# Revit family: Toilet_Seat-Elongated_Closed_Front-KOHLER-EIR-K-79208
name_source: partatom
category: Specialty Equipment
units: mm (PartAtom-declared; Revit-internal decimal feet)

## family parameters
Cut with Voids When Loaded = No
Host = Face
OmniClass Number = 23.31.19.19.17
OmniClass Title = Water Closet Seats
Part Type = Normal
Room Calculation Point = No
Round Connector Dimension = Use Diameter
Shared = No

## types (5) — shared parameters
ADA Compliant = No
Assembly Code = C1030200
Date Modified = 02/27/2023
Default Elevation = 15"
Height = 5 1/16"
Length = 27 5/8"
Manufacturer = Kohler Co.
Master Format 2014 = 10 28 00
Master Format 2014 Name = Toilet, Bath, and Laundry Accessories
Material = Plastic
Product Documentation Link = https://www.us.kohler.com
Product Name = EIR
Product Page URL = http://www.us.kohler.com
URL = https://www.us.kohler.com
WaterSense Certified = No
Width = 16 1/2"

## per-type parameters (varying)
| type | Description | Finish | Model | Secondary Finish | Type |
| 0-White | Intelligent Toilet Seat Cover | Kohler-Plastic-0-White | K-79208-0 | Kohler-Plastic-0-White | 1 |
| 58-Thunder Grey | Intelligent Toilet Seat Cover | Kohler-Plastic-58-Thunder_Grey | K-79208-58 | Kohler-Plastic-58-Thunder_Grey | 2 |
| RGD, 0-White | Elongated Toilet Seat Lid With Accent Band | Kohler-Plastic-0-White | K-79208-RGD-0 | Kohler-Plastic-RGD-Polished_Rose_Gold | 4 |
| SG,0-White | Elongated Toilet Seat Lid With Accent Band | Kohler-Plastic-0-White | K-79208-SG-0 | Kohler-Plastic-SG-Sunrise_Gold | 5 |
| SG-Sunrise Gold | Intelligent Toilet Seat Cover | Kohler-Plastic-SG-Sunrise_Gold | K-79208-SG | Kohler-Plastic-SG-Sunrise_Gold | 3 |

## geometry (parser evidence)
native form markers: Sweep x5
no freeform markers — native parametric forms only
